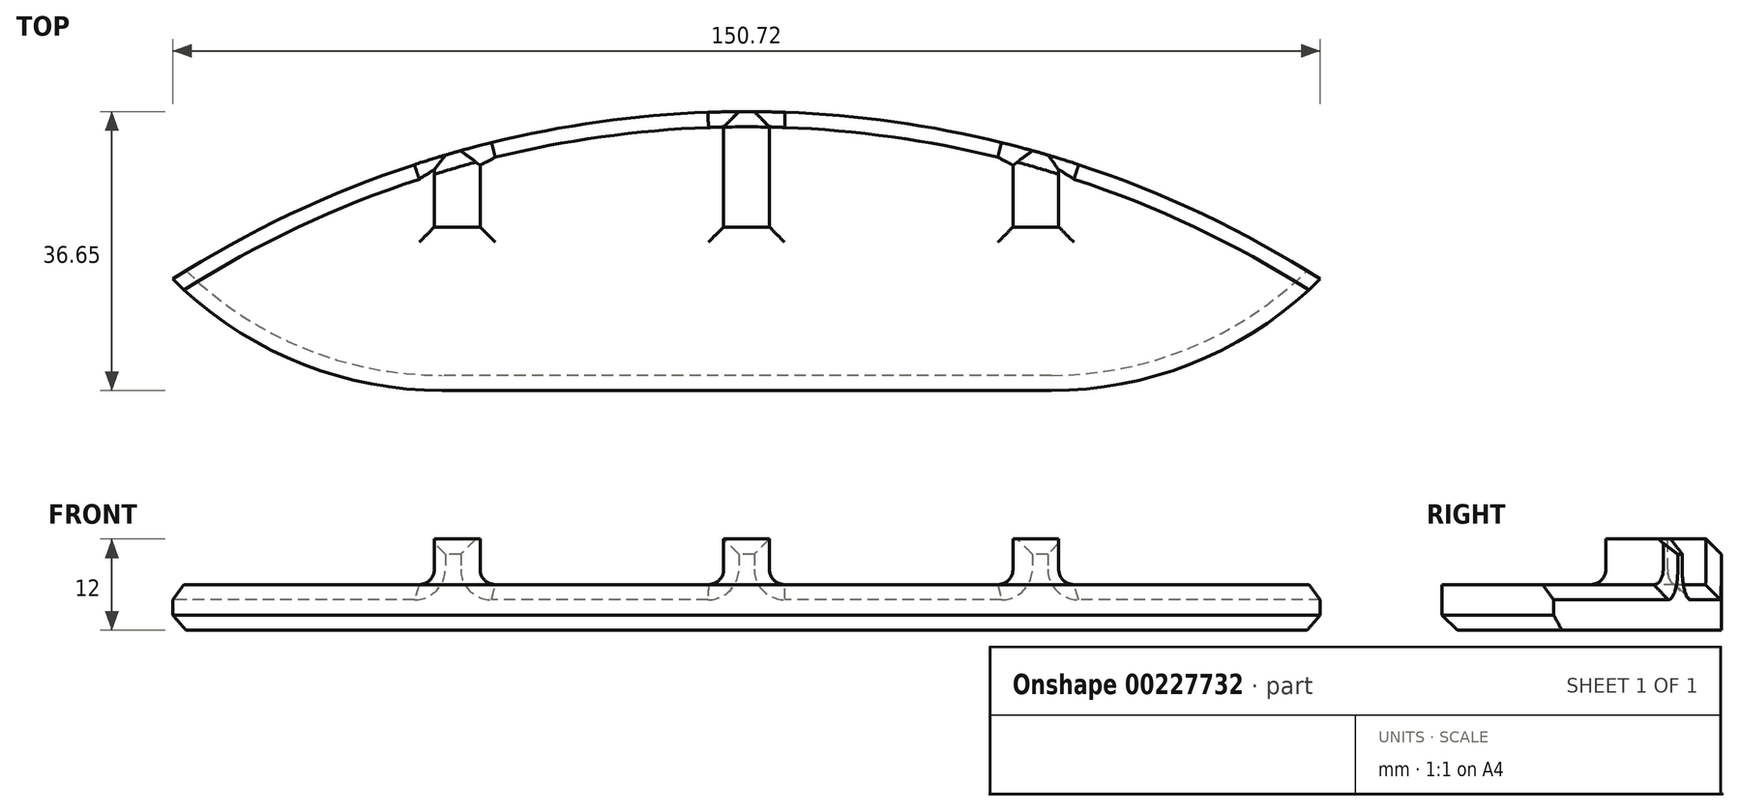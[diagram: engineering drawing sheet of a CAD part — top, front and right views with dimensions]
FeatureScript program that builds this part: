
annotation { "Feature Type Name" : "Feature", "Feature Type Description" : "" }
export const myFeature = defineFeature(function(context is Context, id is Id, definition is map)
    precondition{}
    {
        {
            var Q0;
            Q0=qCreatedBy(makeId("Top.planeOp"),FACE);
            var sketch = newSketch(context, id + "F0", { "sketchPlane" : qUnion([Q0])});
            skCircle(sketch, "E0", {"center": v(-19, 40) * mm, "radius": 2.75 * mm});
            skCircle(sketch, "E1.MirrorC", {"center": v(-19, -40) * mm, "radius": 2.75 * mm});
            skCircle(sketch, "E2.MirrorC", {"center": v(19, 40) * mm, "radius": 2.75 * mm});
            skCircle(sketch, "E3.MirrorC", {"center": v(19, -40) * mm, "radius": 2.75 * mm});
            skLineSegment(sketch, "E4.bottom", {"start": v(90, -90) * mm, "end": v(-90, -90) * mm});
            skLineSegment(sketch, "E4.top", {"start": v(90, 90) * mm, "end": v(-90, 90) * mm});
            skLineSegment(sketch, "E4.left", {"start": v(90, -90) * mm, "end": v(90, 90) * mm});
            skLineSegment(sketch, "E4.right", {"start": v(-90, -90) * mm, "end": v(-90, 90) * mm});
            skPoint(sketch, "E4.middle", {"position": v(0, 0) * mm});
            skLineSegment(sketch, "E5", {"start": v(-77, 74.08) * mm, "end": v(-77, -71.25) * mm, "construction": true});
            skCircle(sketch, "E6", {"center": v(-65, 0) * mm, "radius": 12 * mm, "construction": true});
            skLineSegment(sketch, "E7.MirrorCS", {"start": v(77, 74.08) * mm, "end": v(77, -71.25) * mm, "construction": true});
            skCircle(sketch, "E8", {"center": v(65, 50) * mm, "radius": 12 * mm, "construction": true});
            skCircle(sketch, "E9.MirrorC", {"center": v(65, -50) * mm, "radius": 12 * mm, "construction": true});
            skCircle(sketch, "E10", {"center": v(-65, 0) * mm, "radius": 3.6 * mm});
            skCircle(sketch, "E11", {"center": v(65, 50) * mm, "radius": 2.75 * mm});
            skCircle(sketch, "E12.MirrorC", {"center": v(65, -50) * mm, "radius": 2.75 * mm});
            skSolve(sketch);
        }
        {
            var Q0;
            Q0 = qSketchRegion(id + "F0", true);
            extrude(context, id + "F1", {"entities" : qUnion([Q0]), "depth" : 6 * mm});
        }
        {
            var Q0;
            Q0=makeQuery(id+"F1.opExtrude","SWEPT_EDGE",EDGE,{"disambiguationData":[OSD([sQuery(id+"F0.wireOp",EDGE,"E4.top"),sQuery(id+"F0.wireOp",EDGE,"E4.right")])]});
            var Q1;
            Q1=makeQuery(id+"F1.opExtrude","SWEPT_EDGE",EDGE,{"disambiguationData":[OSD([sQuery(id+"F0.wireOp",EDGE,"E4.top"),sQuery(id+"F0.wireOp",EDGE,"E4.left")])]});
            var Q2;
            Q2=makeQuery(id+"F1.opExtrude","SWEPT_EDGE",EDGE,{"disambiguationData":[OSD([sQuery(id+"F0.wireOp",EDGE,"E4.bottom"),sQuery(id+"F0.wireOp",EDGE,"E4.left")])]});
            var Q3;
            Q3=makeQuery(id+"F1.opExtrude","SWEPT_EDGE",EDGE,{"disambiguationData":[OSD([sQuery(id+"F0.wireOp",EDGE,"E4.bottom"),sQuery(id+"F0.wireOp",EDGE,"E4.right")])]});
            fillet(context, id + "F2", {"entities" : qUnion([Q0, Q1, Q2, Q3]), "radius" : 50 * mm, "tangentPropagation" : true, "allowEdgeOverflow" : false});
        }
        {
            var Q0;
            Q0=makeQuery(id+"F1.opExtrude","CAP_FACE",FACE,{"disambiguationData":[OSD([sQuery(id+"F0.wireOp",EDGE,"E0"),sQuery(id+"F0.wireOp",EDGE,"E1.MirrorC"),sQuery(id+"F0.wireOp",EDGE,"E2.MirrorC"),sQuery(id+"F0.wireOp",EDGE,"E3.MirrorC"),sQuery(id+"F0.wireOp",EDGE,"E4.bottom"),sQuery(id+"F0.wireOp",EDGE,"E4.top"),sQuery(id+"F0.wireOp",EDGE,"E4.left"),sQuery(id+"F0.wireOp",EDGE,"E4.right"),sQuery(id+"F0.wireOp",EDGE,"E10"),sQuery(id+"F0.wireOp",EDGE,"E11"),sQuery(id+"F0.wireOp",EDGE,"E12.MirrorC")])],"isStart":false});
            var sketch = newSketch(context, id + "F3", { "sketchPlane" : qUnion([Q0])});
            skLineSegment(sketch, "E13.bottom", {"start": v(-71, 23.5) * mm, "end": v(-41, 23.5) * mm});
            skLineSegment(sketch, "E13.top", {"start": v(-71, 17.5) * mm, "end": v(-41, 17.5) * mm});
            skLineSegment(sketch, "E13.left", {"start": v(-71, 23.5) * mm, "end": v(-71, 17.5) * mm});
            skLineSegment(sketch, "E13.right", {"start": v(71, 23.5) * mm, "end": v(71, 17.5) * mm});
            skLineSegment(sketch, "E14.bottom", {"start": v(-41, 68.5) * mm, "end": v(-35, 68.5) * mm});
            skLineSegment(sketch, "E14.top", {"start": v(-41, -68.5) * mm, "end": v(-35, -68.5) * mm});
            skLineSegment(sketch, "E14.left", {"start": v(-41, 68.5) * mm, "end": v(-41, 23.5) * mm});
            skLineSegment(sketch, "E14.right", {"start": v(-35, 68.5) * mm, "end": v(-35, 23.5) * mm});
            skLineSegment(sketch, "E15.bottom", {"start": v(-71, -17.5) * mm, "end": v(-41, -17.5) * mm});
            skLineSegment(sketch, "E15.top", {"start": v(-71, -23.5) * mm, "end": v(-41, -23.5) * mm});
            skLineSegment(sketch, "E15.left", {"start": v(-71, -17.5) * mm, "end": v(-71, -23.5) * mm});
            skLineSegment(sketch, "E15.right", {"start": v(71, -17.5) * mm, "end": v(71, -23.5) * mm});
            skLineSegment(sketch, "E16.bottom", {"start": v(-3, 68.5) * mm, "end": v(3, 68.5) * mm});
            skLineSegment(sketch, "E16.top", {"start": v(-3, -68.5) * mm, "end": v(3, -68.5) * mm});
            skLineSegment(sketch, "E16.left", {"start": v(-3, 68.5) * mm, "end": v(-3, 23.5) * mm});
            skLineSegment(sketch, "E16.right", {"start": v(3, 68.5) * mm, "end": v(3, 23.5) * mm});
            skLineSegment(sketch, "E17.bottom", {"start": v(35, 68.5) * mm, "end": v(41, 68.5) * mm});
            skLineSegment(sketch, "E17.top", {"start": v(35, -68.5) * mm, "end": v(41, -68.5) * mm});
            skLineSegment(sketch, "E17.left", {"start": v(35, 68.5) * mm, "end": v(35, 23.5) * mm});
            skLineSegment(sketch, "E17.right", {"start": v(41, 68.5) * mm, "end": v(41, 23.5) * mm});
            skLineSegment(sketch, "E18.trimOffspring", {"start": v(-35, 23.5) * mm, "end": v(-3, 23.5) * mm});
            skLineSegment(sketch, "E19.trimOffspring", {"start": v(-41, 17.5) * mm, "end": v(-41, -17.5) * mm});
            skLineSegment(sketch, "E20.trimOffspring", {"start": v(-35, 17.5) * mm, "end": v(-35, -17.5) * mm});
            skLineSegment(sketch, "E21.trimOffspring", {"start": v(-35, 17.5) * mm, "end": v(-3, 17.5) * mm});
            skLineSegment(sketch, "E22.trimOffspring", {"start": v(-35, -17.5) * mm, "end": v(-3, -17.5) * mm});
            skLineSegment(sketch, "E23.trimOffspring", {"start": v(-41, -23.5) * mm, "end": v(-41, -68.5) * mm});
            skLineSegment(sketch, "E24.trimOffspring", {"start": v(-35, -23.5) * mm, "end": v(-3, -23.5) * mm});
            skLineSegment(sketch, "E25.trimOffspring", {"start": v(-35, -23.5) * mm, "end": v(-35, -68.5) * mm});
            skLineSegment(sketch, "E26.trimOffspring", {"start": v(-3, -23.5) * mm, "end": v(-3, -68.5) * mm});
            skLineSegment(sketch, "E27.trimOffspring", {"start": v(3, -17.5) * mm, "end": v(35, -17.5) * mm});
            skLineSegment(sketch, "E28.trimOffspring", {"start": v(3, -23.5) * mm, "end": v(3, -68.5) * mm});
            skLineSegment(sketch, "E29.trimOffspring", {"start": v(3, -23.5) * mm, "end": v(35, -23.5) * mm});
            skLineSegment(sketch, "E30.trimOffspring", {"start": v(35, -23.5) * mm, "end": v(35, -68.5) * mm});
            skLineSegment(sketch, "E31.trimOffspring", {"start": v(41, -17.5) * mm, "end": v(71, -17.5) * mm});
            skLineSegment(sketch, "E32.trimOffspring", {"start": v(41, -23.5) * mm, "end": v(41, -68.5) * mm});
            skLineSegment(sketch, "E33.trimOffspring", {"start": v(41, -23.5) * mm, "end": v(71, -23.5) * mm});
            skLineSegment(sketch, "E34.trimOffspring", {"start": v(41, 17.5) * mm, "end": v(71, 17.5) * mm});
            skLineSegment(sketch, "E35.trimOffspring", {"start": v(41, 23.5) * mm, "end": v(71, 23.5) * mm});
            skLineSegment(sketch, "E36.trimOffspring", {"start": v(41, 17.5) * mm, "end": v(41, -17.5) * mm});
            skLineSegment(sketch, "E37.trimOffspring", {"start": v(35, 17.5) * mm, "end": v(35, -17.5) * mm});
            skLineSegment(sketch, "E38.trimOffspring", {"start": v(3, 17.5) * mm, "end": v(3, -17.5) * mm});
            skLineSegment(sketch, "E39.trimOffspring", {"start": v(-3, 17.5) * mm, "end": v(-3, -17.5) * mm});
            skLineSegment(sketch, "E40.trimOffspring", {"start": v(3, 23.5) * mm, "end": v(35, 23.5) * mm});
            skLineSegment(sketch, "E41.trimOffspring", {"start": v(3, 17.5) * mm, "end": v(35, 17.5) * mm});
            skCircle(sketch, "E42.0", {"center": v(-65, 0) * mm, "radius": 3.6 * mm, "construction": true});
            skLineSegment(sketch, "E43", {"start": v(-65, 17.5) * mm, "end": v(-65, -17.5) * mm, "construction": true});
            skCircle(sketch, "E44.0", {"center": v(-19, 40) * mm, "radius": 2.75 * mm, "construction": true});
            skCircle(sketch, "E45.0", {"center": v(19, 40) * mm, "radius": 2.75 * mm, "construction": true});
            skLineSegment(sketch, "E46", {"start": v(-35, 40) * mm, "end": v(-3, 40) * mm, "construction": true});
            skLineSegment(sketch, "E47", {"start": v(35, 40) * mm, "end": v(3, 40) * mm, "construction": true});
            skSolve(sketch);
        }
        {
            var Q0;
            Q0 = qSketchRegion(id + "F3", true);
            extrude(context, id + "F4", {"entities" : qUnion([Q0]), "operationType" : NewBodyOperationType.ADD, "depth" : 6 * mm});
        }
        {
            var Q0;
            Q0=makeQuery(id+"F4.opExtrude","CAP_EDGE",EDGE,{"disambiguationData":[OSD([sQuery(id+"F3.wireOp",EDGE,"E13.left")])],"isStart":false});
            var Q1;
            Q1=makeQuery(id+"F4.opExtrude","CAP_EDGE",EDGE,{"disambiguationData":[OSD([sQuery(id+"F3.wireOp",EDGE,"E15.left")])],"isStart":false});
            var Q2;
            Q2=makeQuery(id+"F4.opExtrude","CAP_EDGE",EDGE,{"disambiguationData":[OSD([sQuery(id+"F3.wireOp",EDGE,"E13.right")])],"isStart":false});
            var Q3;
            Q3=makeQuery(id+"F4.opExtrude","CAP_EDGE",EDGE,{"disambiguationData":[OSD([sQuery(id+"F3.wireOp",EDGE,"E15.right")])],"isStart":false});
            chamfer(context, id + "F5", {"entities" : qUnion([Q0, Q1, Q2, Q3]), "chamferType" : ChamferType.TWO_OFFSETS, "width1" : 20 * mm, "oppositeDirection" : false, "width2" : 6 * mm, "tangentPropagation" : true});
        }
        {
            var Q0;
            Q0=makeQuery(id+"F4.opExtrude","CAP_EDGE",EDGE,{"disambiguationData":[OSD([sQuery(id+"F3.wireOp",EDGE,"E13.top")])],"isStart":true});
            var Q1;
            Q1=makeQuery(id+"F4.opExtrude","CAP_EDGE",EDGE,{"disambiguationData":[OSD([sQuery(id+"F3.wireOp",EDGE,"E21.trimOffspring")])],"isStart":true});
            var Q2;
            Q2=makeQuery(id+"F4.opExtrude","CAP_EDGE",EDGE,{"disambiguationData":[OSD([sQuery(id+"F3.wireOp",EDGE,"E20.trimOffspring")])],"isStart":true});
            var Q3;
            Q3=makeQuery(id+"F4.opExtrude","CAP_EDGE",EDGE,{"disambiguationData":[OSD([sQuery(id+"F3.wireOp",EDGE,"E39.trimOffspring")])],"isStart":true});
            var Q4;
            Q4=makeQuery(id+"F4.opExtrude","CAP_EDGE",EDGE,{"disambiguationData":[OSD([sQuery(id+"F3.wireOp",EDGE,"E22.trimOffspring")])],"isStart":true});
            var Q5;
            Q5=makeQuery(id+"F4.opExtrude","CAP_EDGE",EDGE,{"disambiguationData":[OSD([sQuery(id+"F3.wireOp",EDGE,"E41.trimOffspring")])],"isStart":true});
            var Q6;
            Q6=makeQuery(id+"F4.opExtrude","CAP_EDGE",EDGE,{"disambiguationData":[OSD([sQuery(id+"F3.wireOp",EDGE,"E38.trimOffspring")])],"isStart":true});
            var Q7;
            Q7=makeQuery(id+"F4.opExtrude","CAP_EDGE",EDGE,{"disambiguationData":[OSD([sQuery(id+"F3.wireOp",EDGE,"E27.trimOffspring")])],"isStart":true});
            var Q8;
            Q8=makeQuery(id+"F4.opExtrude","CAP_EDGE",EDGE,{"disambiguationData":[OSD([sQuery(id+"F3.wireOp",EDGE,"E37.trimOffspring")])],"isStart":true});
            var Q9;
            Q9=makeQuery(id+"F4.opExtrude","CAP_EDGE",EDGE,{"disambiguationData":[OSD([sQuery(id+"F3.wireOp",EDGE,"E36.trimOffspring")])],"isStart":true});
            var Q10;
            Q10=makeQuery(id+"F4.opExtrude","CAP_EDGE",EDGE,{"disambiguationData":[OSD([sQuery(id+"F3.wireOp",EDGE,"E34.trimOffspring")])],"isStart":true});
            var Q11;
            Q11=makeQuery(id+"F4.opExtrude","CAP_EDGE",EDGE,{"disambiguationData":[OSD([sQuery(id+"F3.wireOp",EDGE,"E31.trimOffspring")])],"isStart":true});
            var Q12;
            Q12=makeQuery(id+"F4.opExtrude","CAP_EDGE",EDGE,{"disambiguationData":[OSD([sQuery(id+"F3.wireOp",EDGE,"E33.trimOffspring")])],"isStart":true});
            var Q13;
            Q13=makeQuery(id+"F4.opExtrude","CAP_EDGE",EDGE,{"disambiguationData":[OSD([sQuery(id+"F3.wireOp",EDGE,"E32.trimOffspring")])],"isStart":true});
            var Q14;
            Q14=makeQuery(id+"F4.opExtrude","CAP_EDGE",EDGE,{"disambiguationData":[OSD([sQuery(id+"F3.wireOp",EDGE,"E17.top")])],"isStart":true});
            var Q15;
            Q15=makeQuery(id+"F4.opExtrude","CAP_EDGE",EDGE,{"disambiguationData":[OSD([sQuery(id+"F3.wireOp",EDGE,"E30.trimOffspring")])],"isStart":true});
            var Q16;
            Q16=makeQuery(id+"F4.opExtrude","CAP_EDGE",EDGE,{"disambiguationData":[OSD([sQuery(id+"F3.wireOp",EDGE,"E29.trimOffspring")])],"isStart":true});
            var Q17;
            Q17=makeQuery(id+"F4.opExtrude","CAP_EDGE",EDGE,{"disambiguationData":[OSD([sQuery(id+"F3.wireOp",EDGE,"E28.trimOffspring")])],"isStart":true});
            var Q18;
            Q18=makeQuery(id+"F4.opExtrude","CAP_EDGE",EDGE,{"disambiguationData":[OSD([sQuery(id+"F3.wireOp",EDGE,"E26.trimOffspring")])],"isStart":true});
            var Q19;
            Q19=makeQuery(id+"F4.opExtrude","CAP_EDGE",EDGE,{"disambiguationData":[OSD([sQuery(id+"F3.wireOp",EDGE,"E24.trimOffspring")])],"isStart":true});
            var Q20;
            Q20=makeQuery(id+"F4.opExtrude","CAP_EDGE",EDGE,{"disambiguationData":[OSD([sQuery(id+"F3.wireOp",EDGE,"E16.top")])],"isStart":true});
            var Q21;
            Q21=makeQuery(id+"F4.opExtrude","CAP_EDGE",EDGE,{"disambiguationData":[OSD([sQuery(id+"F3.wireOp",EDGE,"E14.top")])],"isStart":true});
            var Q22;
            Q22=makeQuery(id+"F4.opExtrude","CAP_EDGE",EDGE,{"disambiguationData":[OSD([sQuery(id+"F3.wireOp",EDGE,"E25.trimOffspring")])],"isStart":true});
            var Q23;
            Q23=makeQuery(id+"F4.opExtrude","CAP_EDGE",EDGE,{"disambiguationData":[OSD([sQuery(id+"F3.wireOp",EDGE,"E23.trimOffspring")])],"isStart":true});
            var Q24;
            Q24=makeQuery(id+"F4.opExtrude","CAP_EDGE",EDGE,{"disambiguationData":[OSD([sQuery(id+"F3.wireOp",EDGE,"E15.top")])],"isStart":true});
            var Q25;
            Q25=makeQuery(id+"F4.opExtrude","CAP_EDGE",EDGE,{"disambiguationData":[OSD([sQuery(id+"F3.wireOp",EDGE,"E15.bottom")])],"isStart":true});
            var Q26;
            Q26=makeQuery(id+"F4.opExtrude","CAP_EDGE",EDGE,{"disambiguationData":[OSD([sQuery(id+"F3.wireOp",EDGE,"E19.trimOffspring")])],"isStart":true});
            var Q27;
            Q27=makeQuery(id+"F4.opExtrude","CAP_EDGE",EDGE,{"disambiguationData":[OSD([sQuery(id+"F3.wireOp",EDGE,"E13.bottom")])],"isStart":true});
            var Q28;
            Q28=makeQuery(id+"F4.opExtrude","CAP_EDGE",EDGE,{"disambiguationData":[OSD([sQuery(id+"F3.wireOp",EDGE,"E14.left")])],"isStart":true});
            var Q29;
            Q29=makeQuery(id+"F4.opExtrude","CAP_EDGE",EDGE,{"disambiguationData":[OSD([sQuery(id+"F3.wireOp",EDGE,"E14.bottom")])],"isStart":true});
            var Q30;
            Q30=makeQuery(id+"F4.opExtrude","CAP_EDGE",EDGE,{"disambiguationData":[OSD([sQuery(id+"F3.wireOp",EDGE,"E16.bottom")])],"isStart":true});
            var Q31;
            Q31=makeQuery(id+"F4.opExtrude","CAP_EDGE",EDGE,{"disambiguationData":[OSD([sQuery(id+"F3.wireOp",EDGE,"E17.bottom")])],"isStart":true});
            var Q32;
            Q32=makeQuery(id+"F4.opExtrude","CAP_EDGE",EDGE,{"disambiguationData":[OSD([sQuery(id+"F3.wireOp",EDGE,"E17.left")])],"isStart":true});
            var Q33;
            Q33=makeQuery(id+"F4.opExtrude","CAP_EDGE",EDGE,{"disambiguationData":[OSD([sQuery(id+"F3.wireOp",EDGE,"E16.left")])],"isStart":true});
            var Q34;
            Q34=makeQuery(id+"F4.opExtrude","CAP_EDGE",EDGE,{"disambiguationData":[OSD([sQuery(id+"F3.wireOp",EDGE,"E18.trimOffspring")])],"isStart":true});
            var Q35;
            Q35=makeQuery(id+"F4.opExtrude","CAP_EDGE",EDGE,{"disambiguationData":[OSD([sQuery(id+"F3.wireOp",EDGE,"E40.trimOffspring")])],"isStart":true});
            var Q36;
            Q36=makeQuery(id+"F4.opExtrude","CAP_EDGE",EDGE,{"disambiguationData":[OSD([sQuery(id+"F3.wireOp",EDGE,"E35.trimOffspring")])],"isStart":true});
            var Q37;
            Q37=makeQuery(id+"F4.opExtrude","CAP_EDGE",EDGE,{"disambiguationData":[OSD([sQuery(id+"F3.wireOp",EDGE,"E14.right")])],"isStart":true});
            var Q38;
            Q38=makeQuery(id+"F4.opExtrude","CAP_EDGE",EDGE,{"disambiguationData":[OSD([sQuery(id+"F3.wireOp",EDGE,"E16.right")])],"isStart":true});
            var Q39;
            Q39=makeQuery(id+"F4.opExtrude","CAP_EDGE",EDGE,{"disambiguationData":[OSD([sQuery(id+"F3.wireOp",EDGE,"E17.right")])],"isStart":true});
            fillet(context, id + "F6", {"entities" : qUnion([Q0, Q1, Q2, Q3, Q4, Q5, Q6, Q7, Q8, Q9, Q10, Q11, Q12, Q13, Q14, Q15, Q16, Q17, Q18, Q19, Q20, Q21, Q22, Q23, Q24, Q25, Q26, Q27, Q28, Q29, Q30, Q31, Q32, Q33, Q34, Q35, Q36, Q37, Q38, Q39]), "radius" : 2 * mm, "tangentPropagation" : true, "allowEdgeOverflow" : false});
        }
        {
            var Q0;
            Q0=makeQuery(id+"F1.opExtrude","CAP_FACE",FACE,{"disambiguationData":[OSD([sQuery(id+"F0.wireOp",EDGE,"E0"),sQuery(id+"F0.wireOp",EDGE,"E1.MirrorC"),sQuery(id+"F0.wireOp",EDGE,"E2.MirrorC"),sQuery(id+"F0.wireOp",EDGE,"E3.MirrorC"),sQuery(id+"F0.wireOp",EDGE,"E4.bottom"),sQuery(id+"F0.wireOp",EDGE,"E4.top"),sQuery(id+"F0.wireOp",EDGE,"E4.left"),sQuery(id+"F0.wireOp",EDGE,"E4.right"),sQuery(id+"F0.wireOp",EDGE,"E10"),sQuery(id+"F0.wireOp",EDGE,"E11"),sQuery(id+"F0.wireOp",EDGE,"E12.MirrorC")])],"isStart":true});
            var sketch = newSketch(context, id + "F7", { "sketchPlane" : qUnion([Q0])});
            skPoint(sketch, "E48.0", {"position": v(-75.36, -75.36) * mm});
            skPoint(sketch, "E49.0", {"position": v(75.36, -75.36) * mm});
            skArc(sketch, "E50", {"start": v(75.36, -75.36) * mm, "mid": v(0, -53.35) * mm, "end": v(-75.36, -75.36) * mm});
            skArc(sketch, "E51.MirrorCS", {"start": v(75.36, 75.36) * mm, "mid": v(0, 53.35) * mm, "end": v(-75.36, 75.36) * mm});
            skSolve(sketch);
        }
        {
            var Q0;
            {var subQ0=sQuery(id+"F7.wireOp",EDGE,"E50");Q0=makeQuery(id+"F7.imprint","IMPRINT",FACE,{"disambiguationData":[TD([[makeQuery(id+"F7.imprint","IMPRINT",EDGE,{"derivedFrom":subQ0}),1.0]])]});}
            var Q1;
            {var subQ0=sQuery(id+"F7.wireOp",EDGE,"E51.MirrorCS");Q1=makeQuery(id+"F7.imprint","IMPRINT",FACE,{"disambiguationData":[TD([[makeQuery(id+"F7.imprint","IMPRINT",EDGE,{"derivedFrom":subQ0}),-1.0]])]});}
            extrude(context, id + "F8", {"entities" : qUnion([Q0, Q1]), "operationType" : NewBodyOperationType.REMOVE, "endBound" : BoundingType.THROUGH_ALL, "oppositeDirection" : true, "depth" : 25 * mm});
        }
        {
            var Q0;
            {var subQ0=sQuery(id+"F0.wireOp",EDGE,"E4.right");var subQ1=sQuery(id+"F0.wireOp",EDGE,"E4.top");Q0=makeQuery(id+"F2.opFillet","BLEND_EDGE",EDGE,{"blendedFrom":[makeQuery(id+"F1.opExtrude","SWEPT_EDGE",EDGE,{"disambiguationData":[OSD([subQ1,subQ0])]}),makeQuery(id+"F1.opExtrude","CAP_FACE",FACE,{"disambiguationData":[OSD([sQuery(id+"F0.wireOp",EDGE,"E0"),sQuery(id+"F0.wireOp",EDGE,"E1.MirrorC"),sQuery(id+"F0.wireOp",EDGE,"E2.MirrorC"),sQuery(id+"F0.wireOp",EDGE,"E3.MirrorC"),sQuery(id+"F0.wireOp",EDGE,"E4.bottom"),subQ1,sQuery(id+"F0.wireOp",EDGE,"E4.left"),subQ0,sQuery(id+"F0.wireOp",EDGE,"E10"),sQuery(id+"F0.wireOp",EDGE,"E11"),sQuery(id+"F0.wireOp",EDGE,"E12.MirrorC")])],"isStart":false})],"blendedInto":[makeQuery(id+"F1.opExtrude","CAP_FACE",FACE,{"disambiguationData":[OSD([sQuery(id+"F0.wireOp",EDGE,"E0"),sQuery(id+"F0.wireOp",EDGE,"E1.MirrorC"),sQuery(id+"F0.wireOp",EDGE,"E2.MirrorC"),sQuery(id+"F0.wireOp",EDGE,"E3.MirrorC"),sQuery(id+"F0.wireOp",EDGE,"E4.bottom"),subQ1,sQuery(id+"F0.wireOp",EDGE,"E4.left"),subQ0,sQuery(id+"F0.wireOp",EDGE,"E10"),sQuery(id+"F0.wireOp",EDGE,"E11"),sQuery(id+"F0.wireOp",EDGE,"E12.MirrorC")])],"isStart":false})]});}
            var Q1;
            {var subQ0=sQuery(id+"F0.wireOp",EDGE,"E4.right");var subQ1=sQuery(id+"F0.wireOp",EDGE,"E4.bottom");Q1=makeQuery(id+"F2.opFillet","BLEND_EDGE",EDGE,{"blendedFrom":[makeQuery(id+"F1.opExtrude","SWEPT_EDGE",EDGE,{"disambiguationData":[OSD([subQ1,subQ0])]}),makeQuery(id+"F1.opExtrude","CAP_FACE",FACE,{"disambiguationData":[OSD([sQuery(id+"F0.wireOp",EDGE,"E0"),sQuery(id+"F0.wireOp",EDGE,"E1.MirrorC"),sQuery(id+"F0.wireOp",EDGE,"E2.MirrorC"),sQuery(id+"F0.wireOp",EDGE,"E3.MirrorC"),subQ1,sQuery(id+"F0.wireOp",EDGE,"E4.top"),sQuery(id+"F0.wireOp",EDGE,"E4.left"),subQ0,sQuery(id+"F0.wireOp",EDGE,"E10"),sQuery(id+"F0.wireOp",EDGE,"E11"),sQuery(id+"F0.wireOp",EDGE,"E12.MirrorC")])],"isStart":true})],"blendedInto":[makeQuery(id+"F1.opExtrude","CAP_FACE",FACE,{"disambiguationData":[OSD([sQuery(id+"F0.wireOp",EDGE,"E0"),sQuery(id+"F0.wireOp",EDGE,"E1.MirrorC"),sQuery(id+"F0.wireOp",EDGE,"E2.MirrorC"),sQuery(id+"F0.wireOp",EDGE,"E3.MirrorC"),subQ1,sQuery(id+"F0.wireOp",EDGE,"E4.top"),sQuery(id+"F0.wireOp",EDGE,"E4.left"),subQ0,sQuery(id+"F0.wireOp",EDGE,"E10"),sQuery(id+"F0.wireOp",EDGE,"E11"),sQuery(id+"F0.wireOp",EDGE,"E12.MirrorC")])],"isStart":true})]});}
            var Q2;
            Q2=makeQuery(id+"F8.boolean.opBoolean","COPY",EDGE,{"derivedFrom":makeQuery(id+"F8.opExtrude","CAP_EDGE",EDGE,{"disambiguationData":[OSD([sQuery(id+"F7.wireOp",EDGE,"hf0Uk4nA-8pbe-iltL-OZs3-23xAQPXPNdW2")])],"isStart":true})});
            var Q3;
            {var subQ0=sQuery(id+"F0.wireOp",EDGE,"E1.MirrorC");var subQ1=sQuery(id+"F0.wireOp",EDGE,"E0");var subQ2=sQuery(id+"F0.wireOp",EDGE,"E11");var subQ3=sQuery(id+"F0.wireOp",EDGE,"E10");var subQ4=sQuery(id+"F0.wireOp",EDGE,"E4.left");var subQ5=sQuery(id+"F0.wireOp",EDGE,"E4.top");var subQ6=sQuery(id+"F0.wireOp",EDGE,"E4.right");var subQ7=sQuery(id+"F0.wireOp",EDGE,"E4.bottom");var subQ8=sQuery(id+"F0.wireOp",EDGE,"E3.MirrorC");var subQ9=sQuery(id+"F0.wireOp",EDGE,"E12.MirrorC");var subQ10=sQuery(id+"F0.wireOp",EDGE,"E2.MirrorC");Q3=makeQuery(id+"F8.boolean.opBoolean","INTERSECT",EDGE,{"disambiguationData":[OD(1.0)],"derivedFrom":[makeQuery(id+"F4.boolean.opBoolean","SPLIT",FACE,{"disambiguationData":[TD([makeQuery(id+"F1.opExtrude","SWEPT_FACE",FACE,{"disambiguationData":[OSD([subQ1])]})])],"derivedFrom":makeQuery(id+"F1.opExtrude","CAP_FACE",FACE,{"disambiguationData":[OSD([subQ1,subQ0,subQ10,subQ8,subQ7,subQ5,subQ4,subQ6,subQ3,subQ2,subQ9])],"isStart":false})}),makeQuery(id+"F8.opExtrude","SWEPT_FACE",FACE,{"disambiguationData":[OSD([sQuery(id+"F7.wireOp",EDGE,"hf0Uk4nA-8pbe-iltL-OZs3-23xAQPXPNdW2")])]})]});}
            var Q4;
            {var subQ0=sQuery(id+"F0.wireOp",EDGE,"E1.MirrorC");var subQ1=sQuery(id+"F0.wireOp",EDGE,"E0");var subQ2=sQuery(id+"F0.wireOp",EDGE,"E11");var subQ3=sQuery(id+"F0.wireOp",EDGE,"E10");var subQ4=sQuery(id+"F0.wireOp",EDGE,"E4.left");var subQ5=sQuery(id+"F0.wireOp",EDGE,"E4.top");var subQ6=sQuery(id+"F0.wireOp",EDGE,"E4.right");var subQ7=sQuery(id+"F0.wireOp",EDGE,"E4.bottom");var subQ8=sQuery(id+"F0.wireOp",EDGE,"E3.MirrorC");var subQ9=sQuery(id+"F0.wireOp",EDGE,"E12.MirrorC");var subQ10=sQuery(id+"F0.wireOp",EDGE,"E2.MirrorC");Q4=makeQuery(id+"F8.boolean.opBoolean","INTERSECT",EDGE,{"disambiguationData":[OD(0.0)],"derivedFrom":[makeQuery(id+"F4.boolean.opBoolean","SPLIT",FACE,{"disambiguationData":[TD([makeQuery(id+"F1.opExtrude","SWEPT_FACE",FACE,{"disambiguationData":[OSD([subQ1])]})])],"derivedFrom":makeQuery(id+"F1.opExtrude","CAP_FACE",FACE,{"disambiguationData":[OSD([subQ1,subQ0,subQ10,subQ8,subQ7,subQ5,subQ4,subQ6,subQ3,subQ2,subQ9])],"isStart":false})}),makeQuery(id+"F8.opExtrude","SWEPT_FACE",FACE,{"disambiguationData":[OSD([sQuery(id+"F7.wireOp",EDGE,"hf0Uk4nA-8pbe-iltL-OZs3-23xAQPXPNdW2")])]})]});}
            var Q5;
            {var subQ0=sQuery(id+"F0.wireOp",EDGE,"E4.left");var subQ1=sQuery(id+"F0.wireOp",EDGE,"E4.top");Q5=makeQuery(id+"F2.opFillet","BLEND_EDGE",EDGE,{"blendedFrom":[makeQuery(id+"F1.opExtrude","SWEPT_EDGE",EDGE,{"disambiguationData":[OSD([subQ1,subQ0])]}),makeQuery(id+"F1.opExtrude","CAP_FACE",FACE,{"disambiguationData":[OSD([sQuery(id+"F0.wireOp",EDGE,"E0"),sQuery(id+"F0.wireOp",EDGE,"E1.MirrorC"),sQuery(id+"F0.wireOp",EDGE,"E2.MirrorC"),sQuery(id+"F0.wireOp",EDGE,"E3.MirrorC"),sQuery(id+"F0.wireOp",EDGE,"E4.bottom"),subQ1,subQ0,sQuery(id+"F0.wireOp",EDGE,"E4.right"),sQuery(id+"F0.wireOp",EDGE,"E10"),sQuery(id+"F0.wireOp",EDGE,"E11"),sQuery(id+"F0.wireOp",EDGE,"E12.MirrorC")])],"isStart":true})],"blendedInto":[makeQuery(id+"F1.opExtrude","CAP_FACE",FACE,{"disambiguationData":[OSD([sQuery(id+"F0.wireOp",EDGE,"E0"),sQuery(id+"F0.wireOp",EDGE,"E1.MirrorC"),sQuery(id+"F0.wireOp",EDGE,"E2.MirrorC"),sQuery(id+"F0.wireOp",EDGE,"E3.MirrorC"),sQuery(id+"F0.wireOp",EDGE,"E4.bottom"),subQ1,subQ0,sQuery(id+"F0.wireOp",EDGE,"E4.right"),sQuery(id+"F0.wireOp",EDGE,"E10"),sQuery(id+"F0.wireOp",EDGE,"E11"),sQuery(id+"F0.wireOp",EDGE,"E12.MirrorC")])],"isStart":true})]});}
            var Q6;
            {var subQ0=sQuery(id+"F0.wireOp",EDGE,"E4.left");var subQ1=sQuery(id+"F0.wireOp",EDGE,"E4.top");Q6=makeQuery(id+"F2.opFillet","BLEND_EDGE",EDGE,{"blendedFrom":[makeQuery(id+"F1.opExtrude","SWEPT_EDGE",EDGE,{"disambiguationData":[OSD([subQ1,subQ0])]}),makeQuery(id+"F1.opExtrude","CAP_FACE",FACE,{"disambiguationData":[OSD([sQuery(id+"F0.wireOp",EDGE,"E0"),sQuery(id+"F0.wireOp",EDGE,"E1.MirrorC"),sQuery(id+"F0.wireOp",EDGE,"E2.MirrorC"),sQuery(id+"F0.wireOp",EDGE,"E3.MirrorC"),sQuery(id+"F0.wireOp",EDGE,"E4.bottom"),subQ1,subQ0,sQuery(id+"F0.wireOp",EDGE,"E4.right"),sQuery(id+"F0.wireOp",EDGE,"E10"),sQuery(id+"F0.wireOp",EDGE,"E11"),sQuery(id+"F0.wireOp",EDGE,"E12.MirrorC")])],"isStart":false})],"blendedInto":[makeQuery(id+"F1.opExtrude","CAP_FACE",FACE,{"disambiguationData":[OSD([sQuery(id+"F0.wireOp",EDGE,"E0"),sQuery(id+"F0.wireOp",EDGE,"E1.MirrorC"),sQuery(id+"F0.wireOp",EDGE,"E2.MirrorC"),sQuery(id+"F0.wireOp",EDGE,"E3.MirrorC"),sQuery(id+"F0.wireOp",EDGE,"E4.bottom"),subQ1,subQ0,sQuery(id+"F0.wireOp",EDGE,"E4.right"),sQuery(id+"F0.wireOp",EDGE,"E10"),sQuery(id+"F0.wireOp",EDGE,"E11"),sQuery(id+"F0.wireOp",EDGE,"E12.MirrorC")])],"isStart":false})]});}
            var Q7;
            Q7=makeQuery(id+"F8.boolean.opBoolean","COPY",EDGE,{"derivedFrom":makeQuery(id+"F8.opExtrude","CAP_EDGE",EDGE,{"disambiguationData":[OSD([sQuery(id+"F7.wireOp",EDGE,"0e658634-30ef-473e-8450-9c662343231f0.MirrorCS")])],"isStart":true})});
            var Q8;
            {var subQ0=sQuery(id+"F0.wireOp",EDGE,"E1.MirrorC");var subQ1=sQuery(id+"F0.wireOp",EDGE,"E0");var subQ2=sQuery(id+"F0.wireOp",EDGE,"E11");var subQ3=sQuery(id+"F0.wireOp",EDGE,"E10");var subQ4=sQuery(id+"F0.wireOp",EDGE,"E4.left");var subQ5=sQuery(id+"F0.wireOp",EDGE,"E4.top");var subQ6=sQuery(id+"F0.wireOp",EDGE,"E4.right");var subQ7=sQuery(id+"F0.wireOp",EDGE,"E4.bottom");var subQ8=sQuery(id+"F0.wireOp",EDGE,"E3.MirrorC");var subQ9=sQuery(id+"F0.wireOp",EDGE,"E12.MirrorC");var subQ10=sQuery(id+"F0.wireOp",EDGE,"E2.MirrorC");Q8=makeQuery(id+"F8.boolean.opBoolean","INTERSECT",EDGE,{"disambiguationData":[OD(0.0)],"derivedFrom":[makeQuery(id+"F4.boolean.opBoolean","SPLIT",FACE,{"disambiguationData":[TD([makeQuery(id+"F1.opExtrude","SWEPT_FACE",FACE,{"disambiguationData":[OSD([subQ1])]})])],"derivedFrom":makeQuery(id+"F1.opExtrude","CAP_FACE",FACE,{"disambiguationData":[OSD([subQ1,subQ0,subQ10,subQ8,subQ7,subQ5,subQ4,subQ6,subQ3,subQ2,subQ9])],"isStart":false})}),makeQuery(id+"F8.opExtrude","SWEPT_FACE",FACE,{"disambiguationData":[OSD([sQuery(id+"F7.wireOp",EDGE,"0e658634-30ef-473e-8450-9c662343231f0.MirrorCS")])]})]});}
            var Q9;
            {var subQ0=sQuery(id+"F0.wireOp",EDGE,"E1.MirrorC");var subQ1=sQuery(id+"F0.wireOp",EDGE,"E0");var subQ2=sQuery(id+"F0.wireOp",EDGE,"E11");var subQ3=sQuery(id+"F0.wireOp",EDGE,"E10");var subQ4=sQuery(id+"F0.wireOp",EDGE,"E4.left");var subQ5=sQuery(id+"F0.wireOp",EDGE,"E4.top");var subQ6=sQuery(id+"F0.wireOp",EDGE,"E4.right");var subQ7=sQuery(id+"F0.wireOp",EDGE,"E4.bottom");var subQ8=sQuery(id+"F0.wireOp",EDGE,"E3.MirrorC");var subQ9=sQuery(id+"F0.wireOp",EDGE,"E12.MirrorC");var subQ10=sQuery(id+"F0.wireOp",EDGE,"E2.MirrorC");Q9=makeQuery(id+"F8.boolean.opBoolean","INTERSECT",EDGE,{"disambiguationData":[OD(1.0)],"derivedFrom":[makeQuery(id+"F4.boolean.opBoolean","SPLIT",FACE,{"disambiguationData":[TD([makeQuery(id+"F1.opExtrude","SWEPT_FACE",FACE,{"disambiguationData":[OSD([subQ1])]})])],"derivedFrom":makeQuery(id+"F1.opExtrude","CAP_FACE",FACE,{"disambiguationData":[OSD([subQ1,subQ0,subQ10,subQ8,subQ7,subQ5,subQ4,subQ6,subQ3,subQ2,subQ9])],"isStart":false})}),makeQuery(id+"F8.opExtrude","SWEPT_FACE",FACE,{"disambiguationData":[OSD([sQuery(id+"F7.wireOp",EDGE,"0e658634-30ef-473e-8450-9c662343231f0.MirrorCS")])]})]});}
            var Q10;
            {var subQ0=sQuery(id+"F0.wireOp",EDGE,"E1.MirrorC");var subQ1=sQuery(id+"F0.wireOp",EDGE,"E0");var subQ2=sQuery(id+"F0.wireOp",EDGE,"E11");var subQ3=sQuery(id+"F0.wireOp",EDGE,"E10");var subQ4=sQuery(id+"F0.wireOp",EDGE,"E4.left");var subQ5=sQuery(id+"F0.wireOp",EDGE,"E4.top");var subQ6=sQuery(id+"F0.wireOp",EDGE,"E4.right");var subQ7=sQuery(id+"F0.wireOp",EDGE,"E4.bottom");var subQ8=sQuery(id+"F0.wireOp",EDGE,"E3.MirrorC");var subQ9=sQuery(id+"F0.wireOp",EDGE,"E12.MirrorC");var subQ10=sQuery(id+"F0.wireOp",EDGE,"E2.MirrorC");Q10=makeQuery(id+"F8.boolean.opBoolean","INTERSECT",EDGE,{"disambiguationData":[OD(0.0)],"derivedFrom":[makeQuery(id+"F4.boolean.opBoolean","SPLIT",FACE,{"disambiguationData":[TD([makeQuery(id+"F1.opExtrude","SWEPT_FACE",FACE,{"disambiguationData":[OSD([subQ1])]})])],"derivedFrom":makeQuery(id+"F1.opExtrude","CAP_FACE",FACE,{"disambiguationData":[OSD([subQ1,subQ0,subQ10,subQ8,subQ7,subQ5,subQ4,subQ6,subQ3,subQ2,subQ9])],"isStart":false})}),makeQuery(id+"F8.opExtrude","SWEPT_FACE",FACE,{"disambiguationData":[OSD([sQuery(id+"F7.wireOp",EDGE,"E51.MirrorCS")])]})]});}
            var Q11;
            Q11=makeQuery(id+"F8.boolean.opBoolean","COPY",EDGE,{"derivedFrom":makeQuery(id+"F8.opExtrude","CAP_EDGE",EDGE,{"disambiguationData":[OSD([sQuery(id+"F7.wireOp",EDGE,"E51.MirrorCS")])],"isStart":true})});
            var Q12;
            Q12=makeQuery(id+"F8.boolean.opBoolean","COPY",EDGE,{"derivedFrom":makeQuery(id+"F8.opExtrude","CAP_EDGE",EDGE,{"disambiguationData":[OSD([sQuery(id+"F7.wireOp",EDGE,"E50")])],"isStart":true})});
            var Q13;
            {var subQ0=sQuery(id+"F0.wireOp",EDGE,"E1.MirrorC");var subQ1=sQuery(id+"F0.wireOp",EDGE,"E0");var subQ2=sQuery(id+"F0.wireOp",EDGE,"E11");var subQ3=sQuery(id+"F0.wireOp",EDGE,"E10");var subQ4=sQuery(id+"F0.wireOp",EDGE,"E4.left");var subQ5=sQuery(id+"F0.wireOp",EDGE,"E4.top");var subQ6=sQuery(id+"F0.wireOp",EDGE,"E4.right");var subQ7=sQuery(id+"F0.wireOp",EDGE,"E4.bottom");var subQ8=sQuery(id+"F0.wireOp",EDGE,"E3.MirrorC");var subQ9=sQuery(id+"F0.wireOp",EDGE,"E12.MirrorC");var subQ10=sQuery(id+"F0.wireOp",EDGE,"E2.MirrorC");Q13=makeQuery(id+"F8.boolean.opBoolean","INTERSECT",EDGE,{"disambiguationData":[OD(0.0)],"derivedFrom":[makeQuery(id+"F4.boolean.opBoolean","SPLIT",FACE,{"disambiguationData":[TD([makeQuery(id+"F1.opExtrude","SWEPT_FACE",FACE,{"disambiguationData":[OSD([subQ1])]})])],"derivedFrom":makeQuery(id+"F1.opExtrude","CAP_FACE",FACE,{"disambiguationData":[OSD([subQ1,subQ0,subQ10,subQ8,subQ7,subQ5,subQ4,subQ6,subQ3,subQ2,subQ9])],"isStart":false})}),makeQuery(id+"F8.opExtrude","SWEPT_FACE",FACE,{"disambiguationData":[OSD([sQuery(id+"F7.wireOp",EDGE,"E50")])]})]});}
            var Q14;
            {var subQ0=sQuery(id+"F0.wireOp",EDGE,"E1.MirrorC");var subQ1=sQuery(id+"F0.wireOp",EDGE,"E0");var subQ2=sQuery(id+"F0.wireOp",EDGE,"E11");var subQ3=sQuery(id+"F0.wireOp",EDGE,"E10");var subQ4=sQuery(id+"F0.wireOp",EDGE,"E4.left");var subQ5=sQuery(id+"F0.wireOp",EDGE,"E4.top");var subQ6=sQuery(id+"F0.wireOp",EDGE,"E4.right");var subQ7=sQuery(id+"F0.wireOp",EDGE,"E4.bottom");var subQ8=sQuery(id+"F0.wireOp",EDGE,"E3.MirrorC");var subQ9=sQuery(id+"F0.wireOp",EDGE,"E12.MirrorC");var subQ10=sQuery(id+"F0.wireOp",EDGE,"E2.MirrorC");Q14=makeQuery(id+"F8.boolean.opBoolean","INTERSECT",EDGE,{"disambiguationData":[OD(3.0)],"derivedFrom":[makeQuery(id+"F4.boolean.opBoolean","SPLIT",FACE,{"disambiguationData":[TD([makeQuery(id+"F1.opExtrude","SWEPT_FACE",FACE,{"disambiguationData":[OSD([subQ1])]})])],"derivedFrom":makeQuery(id+"F1.opExtrude","CAP_FACE",FACE,{"disambiguationData":[OSD([subQ1,subQ0,subQ10,subQ8,subQ7,subQ5,subQ4,subQ6,subQ3,subQ2,subQ9])],"isStart":false})}),makeQuery(id+"F8.opExtrude","SWEPT_FACE",FACE,{"disambiguationData":[OSD([sQuery(id+"F7.wireOp",EDGE,"E50")])]})]});}
            var Q15;
            {var subQ0=sQuery(id+"F0.wireOp",EDGE,"E1.MirrorC");var subQ1=sQuery(id+"F0.wireOp",EDGE,"E0");var subQ2=sQuery(id+"F0.wireOp",EDGE,"E11");var subQ3=sQuery(id+"F0.wireOp",EDGE,"E10");var subQ4=sQuery(id+"F0.wireOp",EDGE,"E4.left");var subQ5=sQuery(id+"F0.wireOp",EDGE,"E4.top");var subQ6=sQuery(id+"F0.wireOp",EDGE,"E4.right");var subQ7=sQuery(id+"F0.wireOp",EDGE,"E4.bottom");var subQ8=sQuery(id+"F0.wireOp",EDGE,"E3.MirrorC");var subQ9=sQuery(id+"F0.wireOp",EDGE,"E12.MirrorC");var subQ10=sQuery(id+"F0.wireOp",EDGE,"E2.MirrorC");Q15=makeQuery(id+"F8.boolean.opBoolean","INTERSECT",EDGE,{"disambiguationData":[OD(2.0)],"derivedFrom":[makeQuery(id+"F4.boolean.opBoolean","SPLIT",FACE,{"disambiguationData":[TD([makeQuery(id+"F1.opExtrude","SWEPT_FACE",FACE,{"disambiguationData":[OSD([subQ1])]})])],"derivedFrom":makeQuery(id+"F1.opExtrude","CAP_FACE",FACE,{"disambiguationData":[OSD([subQ1,subQ0,subQ10,subQ8,subQ7,subQ5,subQ4,subQ6,subQ3,subQ2,subQ9])],"isStart":false})}),makeQuery(id+"F8.opExtrude","SWEPT_FACE",FACE,{"disambiguationData":[OSD([sQuery(id+"F7.wireOp",EDGE,"E50")])]})]});}
            var Q16;
            {var subQ0=sQuery(id+"F0.wireOp",EDGE,"E1.MirrorC");var subQ1=sQuery(id+"F0.wireOp",EDGE,"E0");var subQ2=sQuery(id+"F0.wireOp",EDGE,"E11");var subQ3=sQuery(id+"F0.wireOp",EDGE,"E10");var subQ4=sQuery(id+"F0.wireOp",EDGE,"E4.left");var subQ5=sQuery(id+"F0.wireOp",EDGE,"E4.top");var subQ6=sQuery(id+"F0.wireOp",EDGE,"E4.right");var subQ7=sQuery(id+"F0.wireOp",EDGE,"E4.bottom");var subQ8=sQuery(id+"F0.wireOp",EDGE,"E3.MirrorC");var subQ9=sQuery(id+"F0.wireOp",EDGE,"E12.MirrorC");var subQ10=sQuery(id+"F0.wireOp",EDGE,"E2.MirrorC");Q16=makeQuery(id+"F8.boolean.opBoolean","INTERSECT",EDGE,{"disambiguationData":[OD(1.0)],"derivedFrom":[makeQuery(id+"F4.boolean.opBoolean","SPLIT",FACE,{"disambiguationData":[TD([makeQuery(id+"F1.opExtrude","SWEPT_FACE",FACE,{"disambiguationData":[OSD([subQ1])]})])],"derivedFrom":makeQuery(id+"F1.opExtrude","CAP_FACE",FACE,{"disambiguationData":[OSD([subQ1,subQ0,subQ10,subQ8,subQ7,subQ5,subQ4,subQ6,subQ3,subQ2,subQ9])],"isStart":false})}),makeQuery(id+"F8.opExtrude","SWEPT_FACE",FACE,{"disambiguationData":[OSD([sQuery(id+"F7.wireOp",EDGE,"E50")])]})]});}
            var Q17;
            {var subQ0=sQuery(id+"F0.wireOp",EDGE,"E1.MirrorC");var subQ1=sQuery(id+"F0.wireOp",EDGE,"E0");var subQ2=sQuery(id+"F0.wireOp",EDGE,"E11");var subQ3=sQuery(id+"F0.wireOp",EDGE,"E10");var subQ4=sQuery(id+"F0.wireOp",EDGE,"E4.left");var subQ5=sQuery(id+"F0.wireOp",EDGE,"E4.top");var subQ6=sQuery(id+"F0.wireOp",EDGE,"E4.right");var subQ7=sQuery(id+"F0.wireOp",EDGE,"E4.bottom");var subQ8=sQuery(id+"F0.wireOp",EDGE,"E3.MirrorC");var subQ9=sQuery(id+"F0.wireOp",EDGE,"E12.MirrorC");var subQ10=sQuery(id+"F0.wireOp",EDGE,"E2.MirrorC");Q17=makeQuery(id+"F8.boolean.opBoolean","INTERSECT",EDGE,{"disambiguationData":[OD(3.0)],"derivedFrom":[makeQuery(id+"F4.boolean.opBoolean","SPLIT",FACE,{"disambiguationData":[TD([makeQuery(id+"F1.opExtrude","SWEPT_FACE",FACE,{"disambiguationData":[OSD([subQ1])]})])],"derivedFrom":makeQuery(id+"F1.opExtrude","CAP_FACE",FACE,{"disambiguationData":[OSD([subQ1,subQ0,subQ10,subQ8,subQ7,subQ5,subQ4,subQ6,subQ3,subQ2,subQ9])],"isStart":false})}),makeQuery(id+"F8.opExtrude","SWEPT_FACE",FACE,{"disambiguationData":[OSD([sQuery(id+"F7.wireOp",EDGE,"E51.MirrorCS")])]})]});}
            var Q18;
            {var subQ0=sQuery(id+"F0.wireOp",EDGE,"E1.MirrorC");var subQ1=sQuery(id+"F0.wireOp",EDGE,"E0");var subQ2=sQuery(id+"F0.wireOp",EDGE,"E11");var subQ3=sQuery(id+"F0.wireOp",EDGE,"E10");var subQ4=sQuery(id+"F0.wireOp",EDGE,"E4.left");var subQ5=sQuery(id+"F0.wireOp",EDGE,"E4.top");var subQ6=sQuery(id+"F0.wireOp",EDGE,"E4.right");var subQ7=sQuery(id+"F0.wireOp",EDGE,"E4.bottom");var subQ8=sQuery(id+"F0.wireOp",EDGE,"E3.MirrorC");var subQ9=sQuery(id+"F0.wireOp",EDGE,"E12.MirrorC");var subQ10=sQuery(id+"F0.wireOp",EDGE,"E2.MirrorC");Q18=makeQuery(id+"F8.boolean.opBoolean","INTERSECT",EDGE,{"disambiguationData":[OD(2.0)],"derivedFrom":[makeQuery(id+"F4.boolean.opBoolean","SPLIT",FACE,{"disambiguationData":[TD([makeQuery(id+"F1.opExtrude","SWEPT_FACE",FACE,{"disambiguationData":[OSD([subQ1])]})])],"derivedFrom":makeQuery(id+"F1.opExtrude","CAP_FACE",FACE,{"disambiguationData":[OSD([subQ1,subQ0,subQ10,subQ8,subQ7,subQ5,subQ4,subQ6,subQ3,subQ2,subQ9])],"isStart":false})}),makeQuery(id+"F8.opExtrude","SWEPT_FACE",FACE,{"disambiguationData":[OSD([sQuery(id+"F7.wireOp",EDGE,"E51.MirrorCS")])]})]});}
            var Q19;
            {var subQ0=sQuery(id+"F0.wireOp",EDGE,"E1.MirrorC");var subQ1=sQuery(id+"F0.wireOp",EDGE,"E0");var subQ2=sQuery(id+"F0.wireOp",EDGE,"E11");var subQ3=sQuery(id+"F0.wireOp",EDGE,"E10");var subQ4=sQuery(id+"F0.wireOp",EDGE,"E4.left");var subQ5=sQuery(id+"F0.wireOp",EDGE,"E4.top");var subQ6=sQuery(id+"F0.wireOp",EDGE,"E4.right");var subQ7=sQuery(id+"F0.wireOp",EDGE,"E4.bottom");var subQ8=sQuery(id+"F0.wireOp",EDGE,"E3.MirrorC");var subQ9=sQuery(id+"F0.wireOp",EDGE,"E12.MirrorC");var subQ10=sQuery(id+"F0.wireOp",EDGE,"E2.MirrorC");Q19=makeQuery(id+"F8.boolean.opBoolean","INTERSECT",EDGE,{"disambiguationData":[OD(1.0)],"derivedFrom":[makeQuery(id+"F4.boolean.opBoolean","SPLIT",FACE,{"disambiguationData":[TD([makeQuery(id+"F1.opExtrude","SWEPT_FACE",FACE,{"disambiguationData":[OSD([subQ1])]})])],"derivedFrom":makeQuery(id+"F1.opExtrude","CAP_FACE",FACE,{"disambiguationData":[OSD([subQ1,subQ0,subQ10,subQ8,subQ7,subQ5,subQ4,subQ6,subQ3,subQ2,subQ9])],"isStart":false})}),makeQuery(id+"F8.opExtrude","SWEPT_FACE",FACE,{"disambiguationData":[OSD([sQuery(id+"F7.wireOp",EDGE,"E51.MirrorCS")])]})]});}
            var Q20;
            Q20=makeQuery(id+"F8.boolean.opBoolean","INTERSECT",EDGE,{"disambiguationData":[OD(0.0)],"derivedFrom":[makeQuery(id+"F4.opExtrude","CAP_FACE",FACE,{"disambiguationData":[OSD([sQuery(id+"F3.wireOp",EDGE,"E13.bottom"),sQuery(id+"F3.wireOp",EDGE,"E13.top"),sQuery(id+"F3.wireOp",EDGE,"E13.left"),sQuery(id+"F3.wireOp",EDGE,"E13.right"),sQuery(id+"F3.wireOp",EDGE,"E14.bottom"),sQuery(id+"F3.wireOp",EDGE,"E14.top"),sQuery(id+"F3.wireOp",EDGE,"E14.left"),sQuery(id+"F3.wireOp",EDGE,"E14.right"),sQuery(id+"F3.wireOp",EDGE,"E15.bottom"),sQuery(id+"F3.wireOp",EDGE,"E15.top"),sQuery(id+"F3.wireOp",EDGE,"E15.left"),sQuery(id+"F3.wireOp",EDGE,"E15.right"),sQuery(id+"F3.wireOp",EDGE,"E16.bottom"),sQuery(id+"F3.wireOp",EDGE,"E16.top"),sQuery(id+"F3.wireOp",EDGE,"E16.left"),sQuery(id+"F3.wireOp",EDGE,"E16.right"),sQuery(id+"F3.wireOp",EDGE,"E17.bottom"),sQuery(id+"F3.wireOp",EDGE,"E17.top"),sQuery(id+"F3.wireOp",EDGE,"E17.left"),sQuery(id+"F3.wireOp",EDGE,"E17.right"),sQuery(id+"F3.wireOp",EDGE,"E18.trimOffspring"),sQuery(id+"F3.wireOp",EDGE,"E19.trimOffspring"),sQuery(id+"F3.wireOp",EDGE,"E20.trimOffspring"),sQuery(id+"F3.wireOp",EDGE,"E21.trimOffspring"),sQuery(id+"F3.wireOp",EDGE,"E22.trimOffspring"),sQuery(id+"F3.wireOp",EDGE,"E23.trimOffspring"),sQuery(id+"F3.wireOp",EDGE,"E24.trimOffspring"),sQuery(id+"F3.wireOp",EDGE,"E25.trimOffspring"),sQuery(id+"F3.wireOp",EDGE,"E26.trimOffspring"),sQuery(id+"F3.wireOp",EDGE,"E27.trimOffspring"),sQuery(id+"F3.wireOp",EDGE,"E28.trimOffspring"),sQuery(id+"F3.wireOp",EDGE,"E29.trimOffspring"),sQuery(id+"F3.wireOp",EDGE,"E30.trimOffspring"),sQuery(id+"F3.wireOp",EDGE,"E31.trimOffspring"),sQuery(id+"F3.wireOp",EDGE,"E32.trimOffspring"),sQuery(id+"F3.wireOp",EDGE,"E33.trimOffspring"),sQuery(id+"F3.wireOp",EDGE,"E34.trimOffspring"),sQuery(id+"F3.wireOp",EDGE,"E35.trimOffspring"),sQuery(id+"F3.wireOp",EDGE,"E36.trimOffspring"),sQuery(id+"F3.wireOp",EDGE,"E37.trimOffspring"),sQuery(id+"F3.wireOp",EDGE,"E38.trimOffspring"),sQuery(id+"F3.wireOp",EDGE,"E39.trimOffspring"),sQuery(id+"F3.wireOp",EDGE,"E40.trimOffspring"),sQuery(id+"F3.wireOp",EDGE,"E41.trimOffspring")])],"isStart":false}),makeQuery(id+"F8.opExtrude","SWEPT_FACE",FACE,{"disambiguationData":[OSD([sQuery(id+"F7.wireOp",EDGE,"E51.MirrorCS")])]})]});
            var Q21;
            Q21=makeQuery(id+"F8.boolean.opBoolean","INTERSECT",EDGE,{"disambiguationData":[OD(1.0)],"derivedFrom":[makeQuery(id+"F4.opExtrude","CAP_FACE",FACE,{"disambiguationData":[OSD([sQuery(id+"F3.wireOp",EDGE,"E13.bottom"),sQuery(id+"F3.wireOp",EDGE,"E13.top"),sQuery(id+"F3.wireOp",EDGE,"E13.left"),sQuery(id+"F3.wireOp",EDGE,"E13.right"),sQuery(id+"F3.wireOp",EDGE,"E14.bottom"),sQuery(id+"F3.wireOp",EDGE,"E14.top"),sQuery(id+"F3.wireOp",EDGE,"E14.left"),sQuery(id+"F3.wireOp",EDGE,"E14.right"),sQuery(id+"F3.wireOp",EDGE,"E15.bottom"),sQuery(id+"F3.wireOp",EDGE,"E15.top"),sQuery(id+"F3.wireOp",EDGE,"E15.left"),sQuery(id+"F3.wireOp",EDGE,"E15.right"),sQuery(id+"F3.wireOp",EDGE,"E16.bottom"),sQuery(id+"F3.wireOp",EDGE,"E16.top"),sQuery(id+"F3.wireOp",EDGE,"E16.left"),sQuery(id+"F3.wireOp",EDGE,"E16.right"),sQuery(id+"F3.wireOp",EDGE,"E17.bottom"),sQuery(id+"F3.wireOp",EDGE,"E17.top"),sQuery(id+"F3.wireOp",EDGE,"E17.left"),sQuery(id+"F3.wireOp",EDGE,"E17.right"),sQuery(id+"F3.wireOp",EDGE,"E18.trimOffspring"),sQuery(id+"F3.wireOp",EDGE,"E19.trimOffspring"),sQuery(id+"F3.wireOp",EDGE,"E20.trimOffspring"),sQuery(id+"F3.wireOp",EDGE,"E21.trimOffspring"),sQuery(id+"F3.wireOp",EDGE,"E22.trimOffspring"),sQuery(id+"F3.wireOp",EDGE,"E23.trimOffspring"),sQuery(id+"F3.wireOp",EDGE,"E24.trimOffspring"),sQuery(id+"F3.wireOp",EDGE,"E25.trimOffspring"),sQuery(id+"F3.wireOp",EDGE,"E26.trimOffspring"),sQuery(id+"F3.wireOp",EDGE,"E27.trimOffspring"),sQuery(id+"F3.wireOp",EDGE,"E28.trimOffspring"),sQuery(id+"F3.wireOp",EDGE,"E29.trimOffspring"),sQuery(id+"F3.wireOp",EDGE,"E30.trimOffspring"),sQuery(id+"F3.wireOp",EDGE,"E31.trimOffspring"),sQuery(id+"F3.wireOp",EDGE,"E32.trimOffspring"),sQuery(id+"F3.wireOp",EDGE,"E33.trimOffspring"),sQuery(id+"F3.wireOp",EDGE,"E34.trimOffspring"),sQuery(id+"F3.wireOp",EDGE,"E35.trimOffspring"),sQuery(id+"F3.wireOp",EDGE,"E36.trimOffspring"),sQuery(id+"F3.wireOp",EDGE,"E37.trimOffspring"),sQuery(id+"F3.wireOp",EDGE,"E38.trimOffspring"),sQuery(id+"F3.wireOp",EDGE,"E39.trimOffspring"),sQuery(id+"F3.wireOp",EDGE,"E40.trimOffspring"),sQuery(id+"F3.wireOp",EDGE,"E41.trimOffspring")])],"isStart":false}),makeQuery(id+"F8.opExtrude","SWEPT_FACE",FACE,{"disambiguationData":[OSD([sQuery(id+"F7.wireOp",EDGE,"E51.MirrorCS")])]})]});
            var Q22;
            Q22=makeQuery(id+"F8.boolean.opBoolean","INTERSECT",EDGE,{"disambiguationData":[OD(2.0)],"derivedFrom":[makeQuery(id+"F4.opExtrude","CAP_FACE",FACE,{"disambiguationData":[OSD([sQuery(id+"F3.wireOp",EDGE,"E13.bottom"),sQuery(id+"F3.wireOp",EDGE,"E13.top"),sQuery(id+"F3.wireOp",EDGE,"E13.left"),sQuery(id+"F3.wireOp",EDGE,"E13.right"),sQuery(id+"F3.wireOp",EDGE,"E14.bottom"),sQuery(id+"F3.wireOp",EDGE,"E14.top"),sQuery(id+"F3.wireOp",EDGE,"E14.left"),sQuery(id+"F3.wireOp",EDGE,"E14.right"),sQuery(id+"F3.wireOp",EDGE,"E15.bottom"),sQuery(id+"F3.wireOp",EDGE,"E15.top"),sQuery(id+"F3.wireOp",EDGE,"E15.left"),sQuery(id+"F3.wireOp",EDGE,"E15.right"),sQuery(id+"F3.wireOp",EDGE,"E16.bottom"),sQuery(id+"F3.wireOp",EDGE,"E16.top"),sQuery(id+"F3.wireOp",EDGE,"E16.left"),sQuery(id+"F3.wireOp",EDGE,"E16.right"),sQuery(id+"F3.wireOp",EDGE,"E17.bottom"),sQuery(id+"F3.wireOp",EDGE,"E17.top"),sQuery(id+"F3.wireOp",EDGE,"E17.left"),sQuery(id+"F3.wireOp",EDGE,"E17.right"),sQuery(id+"F3.wireOp",EDGE,"E18.trimOffspring"),sQuery(id+"F3.wireOp",EDGE,"E19.trimOffspring"),sQuery(id+"F3.wireOp",EDGE,"E20.trimOffspring"),sQuery(id+"F3.wireOp",EDGE,"E21.trimOffspring"),sQuery(id+"F3.wireOp",EDGE,"E22.trimOffspring"),sQuery(id+"F3.wireOp",EDGE,"E23.trimOffspring"),sQuery(id+"F3.wireOp",EDGE,"E24.trimOffspring"),sQuery(id+"F3.wireOp",EDGE,"E25.trimOffspring"),sQuery(id+"F3.wireOp",EDGE,"E26.trimOffspring"),sQuery(id+"F3.wireOp",EDGE,"E27.trimOffspring"),sQuery(id+"F3.wireOp",EDGE,"E28.trimOffspring"),sQuery(id+"F3.wireOp",EDGE,"E29.trimOffspring"),sQuery(id+"F3.wireOp",EDGE,"E30.trimOffspring"),sQuery(id+"F3.wireOp",EDGE,"E31.trimOffspring"),sQuery(id+"F3.wireOp",EDGE,"E32.trimOffspring"),sQuery(id+"F3.wireOp",EDGE,"E33.trimOffspring"),sQuery(id+"F3.wireOp",EDGE,"E34.trimOffspring"),sQuery(id+"F3.wireOp",EDGE,"E35.trimOffspring"),sQuery(id+"F3.wireOp",EDGE,"E36.trimOffspring"),sQuery(id+"F3.wireOp",EDGE,"E37.trimOffspring"),sQuery(id+"F3.wireOp",EDGE,"E38.trimOffspring"),sQuery(id+"F3.wireOp",EDGE,"E39.trimOffspring"),sQuery(id+"F3.wireOp",EDGE,"E40.trimOffspring"),sQuery(id+"F3.wireOp",EDGE,"E41.trimOffspring")])],"isStart":false}),makeQuery(id+"F8.opExtrude","SWEPT_FACE",FACE,{"disambiguationData":[OSD([sQuery(id+"F7.wireOp",EDGE,"E51.MirrorCS")])]})]});
            var Q23;
            Q23=makeQuery(id+"F8.boolean.opBoolean","INTERSECT",EDGE,{"disambiguationData":[OD(2.0)],"derivedFrom":[makeQuery(id+"F4.opExtrude","CAP_FACE",FACE,{"disambiguationData":[OSD([sQuery(id+"F3.wireOp",EDGE,"E13.bottom"),sQuery(id+"F3.wireOp",EDGE,"E13.top"),sQuery(id+"F3.wireOp",EDGE,"E13.left"),sQuery(id+"F3.wireOp",EDGE,"E13.right"),sQuery(id+"F3.wireOp",EDGE,"E14.bottom"),sQuery(id+"F3.wireOp",EDGE,"E14.top"),sQuery(id+"F3.wireOp",EDGE,"E14.left"),sQuery(id+"F3.wireOp",EDGE,"E14.right"),sQuery(id+"F3.wireOp",EDGE,"E15.bottom"),sQuery(id+"F3.wireOp",EDGE,"E15.top"),sQuery(id+"F3.wireOp",EDGE,"E15.left"),sQuery(id+"F3.wireOp",EDGE,"E15.right"),sQuery(id+"F3.wireOp",EDGE,"E16.bottom"),sQuery(id+"F3.wireOp",EDGE,"E16.top"),sQuery(id+"F3.wireOp",EDGE,"E16.left"),sQuery(id+"F3.wireOp",EDGE,"E16.right"),sQuery(id+"F3.wireOp",EDGE,"E17.bottom"),sQuery(id+"F3.wireOp",EDGE,"E17.top"),sQuery(id+"F3.wireOp",EDGE,"E17.left"),sQuery(id+"F3.wireOp",EDGE,"E17.right"),sQuery(id+"F3.wireOp",EDGE,"E18.trimOffspring"),sQuery(id+"F3.wireOp",EDGE,"E19.trimOffspring"),sQuery(id+"F3.wireOp",EDGE,"E20.trimOffspring"),sQuery(id+"F3.wireOp",EDGE,"E21.trimOffspring"),sQuery(id+"F3.wireOp",EDGE,"E22.trimOffspring"),sQuery(id+"F3.wireOp",EDGE,"E23.trimOffspring"),sQuery(id+"F3.wireOp",EDGE,"E24.trimOffspring"),sQuery(id+"F3.wireOp",EDGE,"E25.trimOffspring"),sQuery(id+"F3.wireOp",EDGE,"E26.trimOffspring"),sQuery(id+"F3.wireOp",EDGE,"E27.trimOffspring"),sQuery(id+"F3.wireOp",EDGE,"E28.trimOffspring"),sQuery(id+"F3.wireOp",EDGE,"E29.trimOffspring"),sQuery(id+"F3.wireOp",EDGE,"E30.trimOffspring"),sQuery(id+"F3.wireOp",EDGE,"E31.trimOffspring"),sQuery(id+"F3.wireOp",EDGE,"E32.trimOffspring"),sQuery(id+"F3.wireOp",EDGE,"E33.trimOffspring"),sQuery(id+"F3.wireOp",EDGE,"E34.trimOffspring"),sQuery(id+"F3.wireOp",EDGE,"E35.trimOffspring"),sQuery(id+"F3.wireOp",EDGE,"E36.trimOffspring"),sQuery(id+"F3.wireOp",EDGE,"E37.trimOffspring"),sQuery(id+"F3.wireOp",EDGE,"E38.trimOffspring"),sQuery(id+"F3.wireOp",EDGE,"E39.trimOffspring"),sQuery(id+"F3.wireOp",EDGE,"E40.trimOffspring"),sQuery(id+"F3.wireOp",EDGE,"E41.trimOffspring")])],"isStart":false}),makeQuery(id+"F8.opExtrude","SWEPT_FACE",FACE,{"disambiguationData":[OSD([sQuery(id+"F7.wireOp",EDGE,"E50")])]})]});
            var Q24;
            Q24=makeQuery(id+"F8.boolean.opBoolean","INTERSECT",EDGE,{"disambiguationData":[OD(1.0)],"derivedFrom":[makeQuery(id+"F4.opExtrude","CAP_FACE",FACE,{"disambiguationData":[OSD([sQuery(id+"F3.wireOp",EDGE,"E13.bottom"),sQuery(id+"F3.wireOp",EDGE,"E13.top"),sQuery(id+"F3.wireOp",EDGE,"E13.left"),sQuery(id+"F3.wireOp",EDGE,"E13.right"),sQuery(id+"F3.wireOp",EDGE,"E14.bottom"),sQuery(id+"F3.wireOp",EDGE,"E14.top"),sQuery(id+"F3.wireOp",EDGE,"E14.left"),sQuery(id+"F3.wireOp",EDGE,"E14.right"),sQuery(id+"F3.wireOp",EDGE,"E15.bottom"),sQuery(id+"F3.wireOp",EDGE,"E15.top"),sQuery(id+"F3.wireOp",EDGE,"E15.left"),sQuery(id+"F3.wireOp",EDGE,"E15.right"),sQuery(id+"F3.wireOp",EDGE,"E16.bottom"),sQuery(id+"F3.wireOp",EDGE,"E16.top"),sQuery(id+"F3.wireOp",EDGE,"E16.left"),sQuery(id+"F3.wireOp",EDGE,"E16.right"),sQuery(id+"F3.wireOp",EDGE,"E17.bottom"),sQuery(id+"F3.wireOp",EDGE,"E17.top"),sQuery(id+"F3.wireOp",EDGE,"E17.left"),sQuery(id+"F3.wireOp",EDGE,"E17.right"),sQuery(id+"F3.wireOp",EDGE,"E18.trimOffspring"),sQuery(id+"F3.wireOp",EDGE,"E19.trimOffspring"),sQuery(id+"F3.wireOp",EDGE,"E20.trimOffspring"),sQuery(id+"F3.wireOp",EDGE,"E21.trimOffspring"),sQuery(id+"F3.wireOp",EDGE,"E22.trimOffspring"),sQuery(id+"F3.wireOp",EDGE,"E23.trimOffspring"),sQuery(id+"F3.wireOp",EDGE,"E24.trimOffspring"),sQuery(id+"F3.wireOp",EDGE,"E25.trimOffspring"),sQuery(id+"F3.wireOp",EDGE,"E26.trimOffspring"),sQuery(id+"F3.wireOp",EDGE,"E27.trimOffspring"),sQuery(id+"F3.wireOp",EDGE,"E28.trimOffspring"),sQuery(id+"F3.wireOp",EDGE,"E29.trimOffspring"),sQuery(id+"F3.wireOp",EDGE,"E30.trimOffspring"),sQuery(id+"F3.wireOp",EDGE,"E31.trimOffspring"),sQuery(id+"F3.wireOp",EDGE,"E32.trimOffspring"),sQuery(id+"F3.wireOp",EDGE,"E33.trimOffspring"),sQuery(id+"F3.wireOp",EDGE,"E34.trimOffspring"),sQuery(id+"F3.wireOp",EDGE,"E35.trimOffspring"),sQuery(id+"F3.wireOp",EDGE,"E36.trimOffspring"),sQuery(id+"F3.wireOp",EDGE,"E37.trimOffspring"),sQuery(id+"F3.wireOp",EDGE,"E38.trimOffspring"),sQuery(id+"F3.wireOp",EDGE,"E39.trimOffspring"),sQuery(id+"F3.wireOp",EDGE,"E40.trimOffspring"),sQuery(id+"F3.wireOp",EDGE,"E41.trimOffspring")])],"isStart":false}),makeQuery(id+"F8.opExtrude","SWEPT_FACE",FACE,{"disambiguationData":[OSD([sQuery(id+"F7.wireOp",EDGE,"E50")])]})]});
            var Q25;
            Q25=makeQuery(id+"F8.boolean.opBoolean","INTERSECT",EDGE,{"disambiguationData":[OD(0.0)],"derivedFrom":[makeQuery(id+"F4.opExtrude","CAP_FACE",FACE,{"disambiguationData":[OSD([sQuery(id+"F3.wireOp",EDGE,"E13.bottom"),sQuery(id+"F3.wireOp",EDGE,"E13.top"),sQuery(id+"F3.wireOp",EDGE,"E13.left"),sQuery(id+"F3.wireOp",EDGE,"E13.right"),sQuery(id+"F3.wireOp",EDGE,"E14.bottom"),sQuery(id+"F3.wireOp",EDGE,"E14.top"),sQuery(id+"F3.wireOp",EDGE,"E14.left"),sQuery(id+"F3.wireOp",EDGE,"E14.right"),sQuery(id+"F3.wireOp",EDGE,"E15.bottom"),sQuery(id+"F3.wireOp",EDGE,"E15.top"),sQuery(id+"F3.wireOp",EDGE,"E15.left"),sQuery(id+"F3.wireOp",EDGE,"E15.right"),sQuery(id+"F3.wireOp",EDGE,"E16.bottom"),sQuery(id+"F3.wireOp",EDGE,"E16.top"),sQuery(id+"F3.wireOp",EDGE,"E16.left"),sQuery(id+"F3.wireOp",EDGE,"E16.right"),sQuery(id+"F3.wireOp",EDGE,"E17.bottom"),sQuery(id+"F3.wireOp",EDGE,"E17.top"),sQuery(id+"F3.wireOp",EDGE,"E17.left"),sQuery(id+"F3.wireOp",EDGE,"E17.right"),sQuery(id+"F3.wireOp",EDGE,"E18.trimOffspring"),sQuery(id+"F3.wireOp",EDGE,"E19.trimOffspring"),sQuery(id+"F3.wireOp",EDGE,"E20.trimOffspring"),sQuery(id+"F3.wireOp",EDGE,"E21.trimOffspring"),sQuery(id+"F3.wireOp",EDGE,"E22.trimOffspring"),sQuery(id+"F3.wireOp",EDGE,"E23.trimOffspring"),sQuery(id+"F3.wireOp",EDGE,"E24.trimOffspring"),sQuery(id+"F3.wireOp",EDGE,"E25.trimOffspring"),sQuery(id+"F3.wireOp",EDGE,"E26.trimOffspring"),sQuery(id+"F3.wireOp",EDGE,"E27.trimOffspring"),sQuery(id+"F3.wireOp",EDGE,"E28.trimOffspring"),sQuery(id+"F3.wireOp",EDGE,"E29.trimOffspring"),sQuery(id+"F3.wireOp",EDGE,"E30.trimOffspring"),sQuery(id+"F3.wireOp",EDGE,"E31.trimOffspring"),sQuery(id+"F3.wireOp",EDGE,"E32.trimOffspring"),sQuery(id+"F3.wireOp",EDGE,"E33.trimOffspring"),sQuery(id+"F3.wireOp",EDGE,"E34.trimOffspring"),sQuery(id+"F3.wireOp",EDGE,"E35.trimOffspring"),sQuery(id+"F3.wireOp",EDGE,"E36.trimOffspring"),sQuery(id+"F3.wireOp",EDGE,"E37.trimOffspring"),sQuery(id+"F3.wireOp",EDGE,"E38.trimOffspring"),sQuery(id+"F3.wireOp",EDGE,"E39.trimOffspring"),sQuery(id+"F3.wireOp",EDGE,"E40.trimOffspring"),sQuery(id+"F3.wireOp",EDGE,"E41.trimOffspring")])],"isStart":false}),makeQuery(id+"F8.opExtrude","SWEPT_FACE",FACE,{"disambiguationData":[OSD([sQuery(id+"F7.wireOp",EDGE,"E50")])]})]});
            chamfer(context, id + "F9", {"entities" : qUnion([Q0, Q1, Q2, Q3, Q4, Q5, Q6, Q7, Q8, Q9, Q10, Q11, Q12, Q13, Q14, Q15, Q16, Q17, Q18, Q19, Q20, Q21, Q22, Q23, Q24, Q25]), "width" : 2 * mm, "tangentPropagation" : true});
        }
    });
